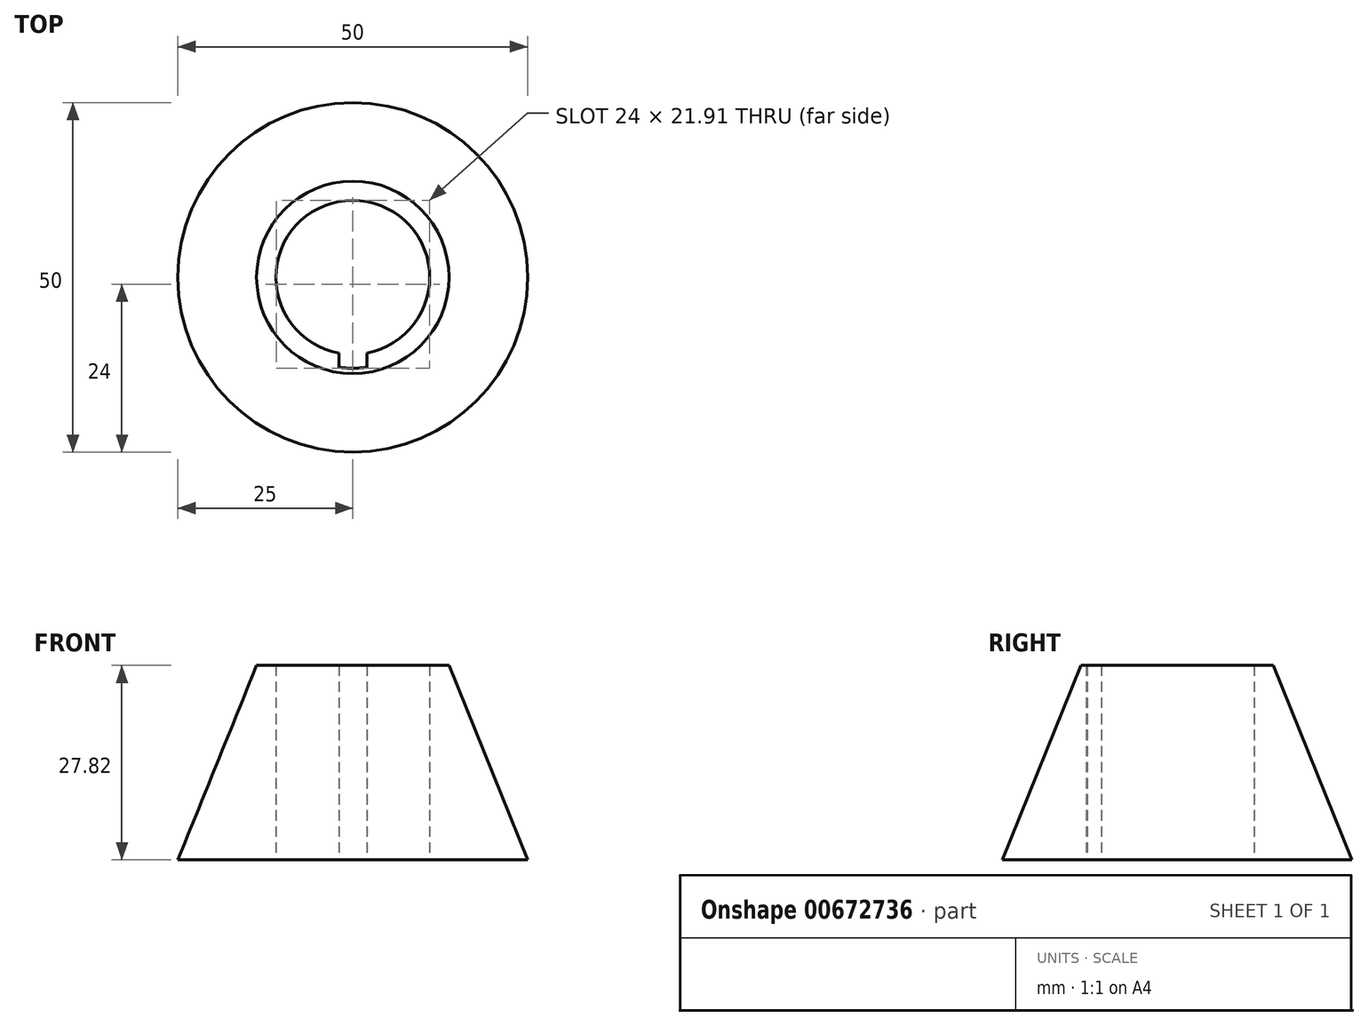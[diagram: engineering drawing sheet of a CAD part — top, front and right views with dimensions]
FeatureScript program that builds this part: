
annotation { "Feature Type Name" : "Feature", "Feature Type Description" : "" }
export const myFeature = defineFeature(function(context is Context, id is Id, definition is map)
    precondition{}
    {
        {
            var Q0;
            Q0=qCreatedBy(makeId("Front.planeOp"),FACE);
            var sketch = newSketch(context, id + "F0", { "sketchPlane" : qUnion([Q0])});
            skLineSegment(sketch, "E0", {"start": v(0, 0) * mm, "end": v(0, 56.83) * mm, "construction": true});
            skLineSegment(sketch, "E1", {"start": v(11, 0) * mm, "end": v(25, 0) * mm});
            skLineSegment(sketch, "E2", {"start": v(11, 27.82) * mm, "end": v(13.76, 27.82) * mm});
            skLineSegment(sketch, "E3", {"start": v(13.76, 27.82) * mm, "end": v(25, 0) * mm});
            skPoint(sketch, "E4.orphan", {"position": v(-25, 0) * mm});
            skLineSegment(sketch, "E5", {"start": v(11, 27.82) * mm, "end": v(11, 0) * mm});
            skSolve(sketch);
        }
        {
            var Q0;
            Q0=makeQuery(id+"F0.imprint","IMPRINT",FACE,{"disambiguationData":[TD([[makeQuery(id+"F0.imprint","IMPRINT",EDGE,{"derivedFrom":sQuery(id+"F0.wireOp",EDGE,"E1")}),1.0]])]});
            var Q1;
            Q1=sQuery(id+"F0.wireOp",EDGE,"E0");
            revolve(context, id + "F1", {"entities" : qUnion([Q0]), "axis" : qUnion([Q1]), "revolveType" : RevolveType.FULL});
        }
        {
            var Q0;
            Q0=makeQuery(id+"F1.opRevolve","SWEPT_FACE",FACE,{"disambiguationData":[OSD([sQuery(id+"F0.wireOp",EDGE,"E1")])]});
            var sketch = newSketch(context, id + "F2", { "sketchPlane" : qUnion([Q0])});
            skArc(sketch, "E6.0", {"start": v(2, 12.85) * mm, "mid": v(0, 13) * mm, "end": v(-2, 12.85) * mm});
            skLineSegment(sketch, "E7", {"start": v(-2, 12.85) * mm, "end": v(-2, 10.82) * mm});
            skLineSegment(sketch, "E8", {"start": v(2, 12.85) * mm, "end": v(2, 10.82) * mm});
            skArc(sketch, "E9.0", {"start": v(2, 10.82) * mm, "mid": v(0, 11) * mm, "end": v(-2, 10.82) * mm});
            skSolve(sketch);
        }
        {
            var Q0;
            Q0 = qSketchRegion(id + "F2", true);
            extrude(context, id + "F3", {"entities" : qUnion([Q0]), "operationType" : NewBodyOperationType.REMOVE, "endBound" : BoundingType.UP_TO_NEXT, "oppositeDirection" : true, "depth" : 25 * mm, "offsetDistance" : 25 * mm});
        }
    });
